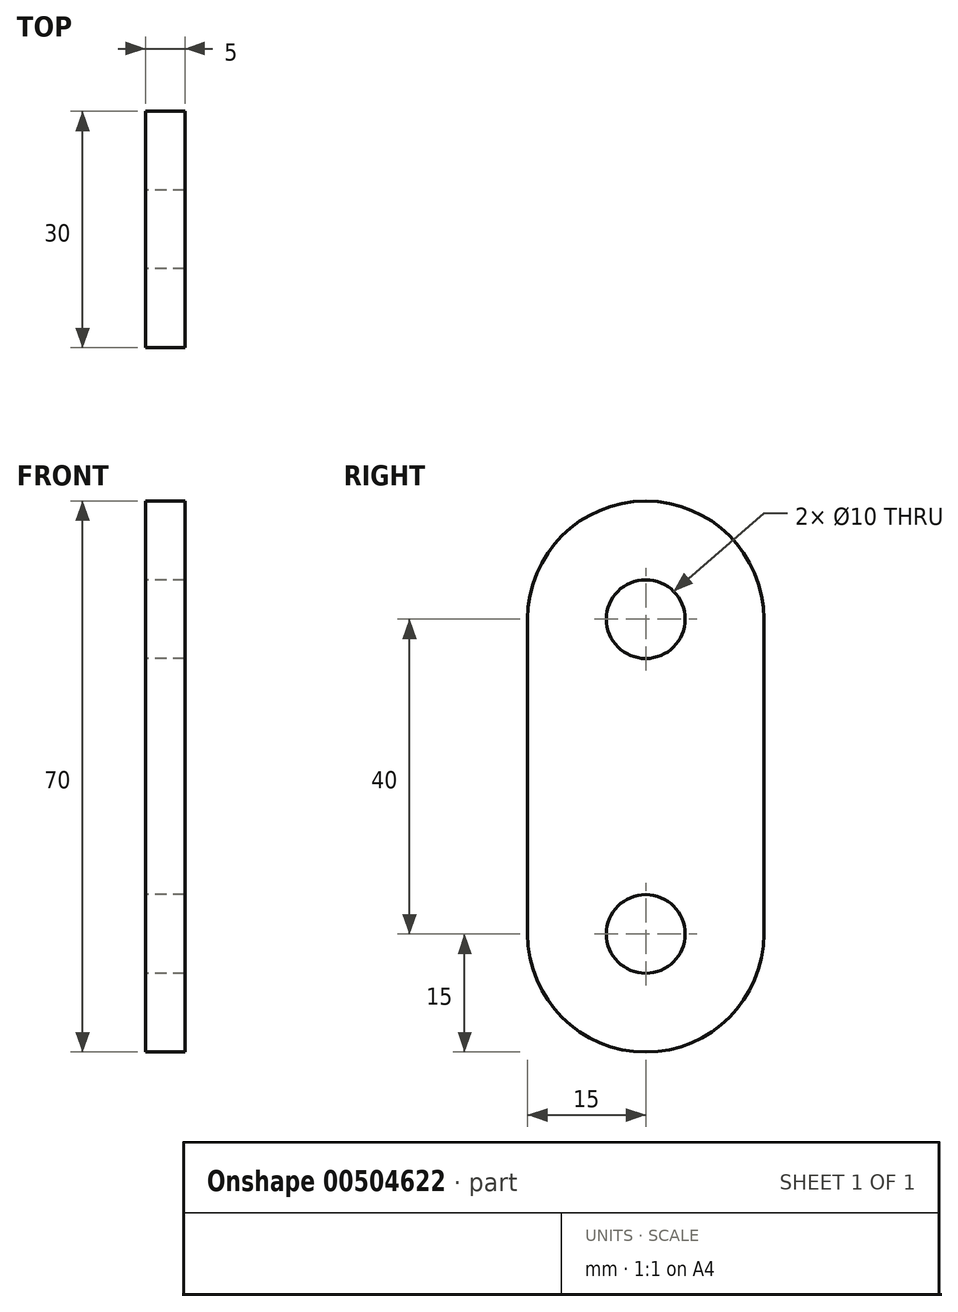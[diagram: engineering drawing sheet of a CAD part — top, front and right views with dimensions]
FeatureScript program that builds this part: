
annotation { "Feature Type Name" : "Feature", "Feature Type Description" : "" }
export const myFeature = defineFeature(function(context is Context, id is Id, definition is map)
    precondition{}
    {
        {
            var Q0;
            Q0=qCreatedBy(makeId("Right.planeOp"),FACE);
            var sketch = newSketch(context, id + "F0", { "sketchPlane" : qUnion([Q0])});
            skCircle(sketch, "E0", {"center": v(0, 0) * mm, "radius": 5 * mm});
            skArc(sketch, "E1", {"start": v(-15, 0) * mm, "mid": v(0, -15) * mm, "end": v(15, 0) * mm});
            skLineSegment(sketch, "E2", {"start": v(0, 0) * mm, "end": v(5, 0) * mm});
            skLineSegment(sketch, "E3", {"start": v(-15, 0) * mm, "end": v(-15, 40) * mm});
            skLineSegment(sketch, "E4", {"start": v(15, 0) * mm, "end": v(15, 40) * mm});
            skCircle(sketch, "E5", {"center": v(0, 40) * mm, "radius": 5 * mm});
            skArc(sketch, "E6", {"start": v(15, 40) * mm, "mid": v(0, 55) * mm, "end": v(-15, 40) * mm});
            skLineSegment(sketch, "E7", {"start": v(0, 0) * mm, "end": v(15, 0) * mm});
            skLineSegment(sketch, "E8", {"start": v(0, 40) * mm, "end": v(15, 40) * mm});
            skLineSegment(sketch, "E9", {"start": v(-15, 40) * mm, "end": v(15, 40) * mm});
            skSolve(sketch);
        }
        {
            var Q0;
            Q0=qSketchRegion(id+"F0",true);
            extrude(context, id + "F1", {"entities" : qUnion([Q0]), "depth" : 5 * mm});
        }
    });
